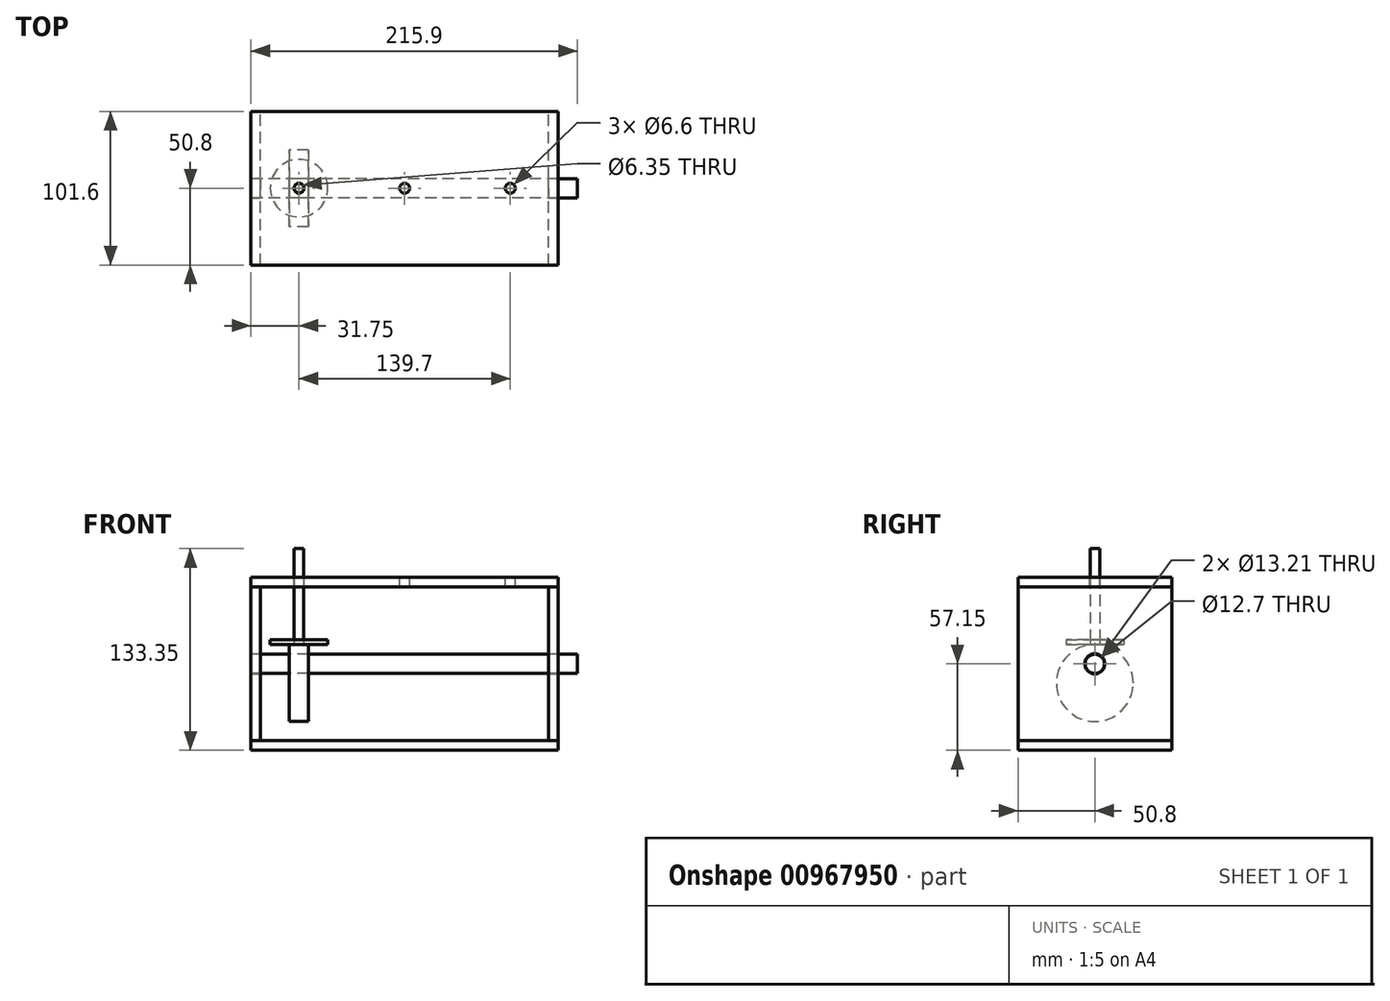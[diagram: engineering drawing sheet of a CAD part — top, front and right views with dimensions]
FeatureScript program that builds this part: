
annotation { "Feature Type Name" : "Feature", "Feature Type Description" : "" }
export const myFeature = defineFeature(function(context is Context, id is Id, definition is map)
    precondition{}
    {
        {
            assignVariable(context, id + "F0", {"name" : "thickness", "anyValue" : 101.6 * mm});
        }
        {
            var Q0;
            Q0=qCreatedBy(makeId("Front.planeOp"),FACE);
            var sketch = newSketch(context, id + "F1", { "sketchPlane" : qUnion([Q0])});
            skLineSegment(sketch, "E0.bottom", {"start": v(-101.6, 6.35) * mm, "end": v(101.6, 6.35) * mm});
            skLineSegment(sketch, "E0.top", {"start": v(-101.6, 0) * mm, "end": v(101.6, 0) * mm});
            skLineSegment(sketch, "E0.left", {"start": v(-101.6, 6.35) * mm, "end": v(-101.6, 0) * mm});
            skLineSegment(sketch, "E0.right", {"start": v(101.6, 6.35) * mm, "end": v(101.6, 0) * mm});
            skLineSegment(sketch, "E1", {"start": v(-101.6, 6.35) * mm, "end": v(-101.6, 107.95) * mm});
            skLineSegment(sketch, "E2", {"start": v(-101.6, 107.95) * mm, "end": v(101.6, 107.95) * mm});
            skLineSegment(sketch, "E3", {"start": v(101.6, 107.95) * mm, "end": v(101.6, 6.35) * mm});
            skLineSegment(sketch, "E4", {"start": v(-95.25, 6.35) * mm, "end": v(-95.25, 107.95) * mm});
            skLineSegment(sketch, "E5", {"start": v(95.25, 6.35) * mm, "end": v(95.25, 107.95) * mm});
            skLineSegment(sketch, "E6", {"start": v(-95.25, 57.15) * mm, "end": v(-101.6, 57.15) * mm, "construction": true});
            skLineSegment(sketch, "E7", {"start": v(95.25, 57.15) * mm, "end": v(101.6, 57.15) * mm, "construction": true});
            skLineSegment(sketch, "E8", {"start": v(-101.6, 107.95) * mm, "end": v(-101.6, 114.3) * mm});
            skLineSegment(sketch, "E9", {"start": v(-101.6, 114.3) * mm, "end": v(101.6, 114.3) * mm});
            skLineSegment(sketch, "E10", {"start": v(101.6, 114.3) * mm, "end": v(101.6, 107.95) * mm});
            skLineSegment(sketch, "E11", {"start": v(-95.25, 57.15) * mm, "end": v(-69.85, 57.15) * mm});
            skLineSegment(sketch, "E12", {"start": v(-69.85, 57.15) * mm, "end": v(0, 57.15) * mm});
            skLineSegment(sketch, "E13", {"start": v(0, 57.15) * mm, "end": v(69.85, 57.15) * mm});
            skLineSegment(sketch, "E14", {"start": v(69.85, 57.15) * mm, "end": v(95.25, 57.15) * mm});
            skLineSegment(sketch, "E15", {"start": v(-69.85, 57.15) * mm, "end": v(-69.85, 44.45) * mm, "construction": true});
            skLineSegment(sketch, "E16", {"start": v(0, 63.5) * mm, "end": v(0, 57.15) * mm, "construction": true});
            skLineSegment(sketch, "E17", {"start": v(69.85, 57.15) * mm, "end": v(69.85, 63.5) * mm, "construction": true});
            skLineSegment(sketch, "E18.bottom", {"start": v(-63.5, 69.85) * mm, "end": v(-76.2, 69.85) * mm});
            skLineSegment(sketch, "E18.top", {"start": v(-63.5, 19.05) * mm, "end": v(-76.2, 19.05) * mm});
            skLineSegment(sketch, "E18.left", {"start": v(-63.5, 69.85) * mm, "end": v(-63.5, 19.05) * mm});
            skLineSegment(sketch, "E18.right", {"start": v(-76.2, 69.85) * mm, "end": v(-76.2, 19.05) * mm});
            skPoint(sketch, "E18.middle", {"position": v(-69.85, 44.45) * mm});
            skLineSegment(sketch, "E19.bottom", {"start": v(6.35, 38.1) * mm, "end": v(-6.35, 38.1) * mm});
            skLineSegment(sketch, "E19.top", {"start": v(6.35, 88.9) * mm, "end": v(-6.35, 88.9) * mm});
            skLineSegment(sketch, "E19.left", {"start": v(6.35, 38.1) * mm, "end": v(6.35, 88.9) * mm});
            skLineSegment(sketch, "E19.right", {"start": v(-6.35, 38.1) * mm, "end": v(-6.35, 88.9) * mm});
            skPoint(sketch, "E19.middle", {"position": v(0, 63.5) * mm});
            skLineSegment(sketch, "E20.bottom", {"start": v(63.5, 38.1) * mm, "end": v(76.2, 38.1) * mm});
            skLineSegment(sketch, "E20.top", {"start": v(63.5, 88.9) * mm, "end": v(76.2, 88.9) * mm});
            skLineSegment(sketch, "E20.left", {"start": v(63.5, 38.1) * mm, "end": v(63.5, 88.9) * mm});
            skLineSegment(sketch, "E20.right", {"start": v(76.2, 38.1) * mm, "end": v(76.2, 88.9) * mm});
            skPoint(sketch, "E20.middle", {"position": v(69.85, 63.5) * mm});
            skLineSegment(sketch, "E21", {"start": v(-76.2, 44.45) * mm, "end": v(-63.5, 44.45) * mm});
            skLineSegment(sketch, "E22", {"start": v(-6.35, 63.5) * mm, "end": v(6.35, 63.5) * mm});
            skLineSegment(sketch, "E23", {"start": v(63.5, 63.5) * mm, "end": v(76.2, 63.5) * mm});
            skLineSegment(sketch, "E24", {"start": v(-69.85, 69.85) * mm, "end": v(-69.85, 133.35) * mm, "construction": true});
            skLineSegment(sketch, "E25", {"start": v(0, 88.9) * mm, "end": v(0, 152.4) * mm, "construction": true});
            skLineSegment(sketch, "E26", {"start": v(69.85, 88.9) * mm, "end": v(69.85, 152.4) * mm, "construction": true});
            skSolve(sketch);
        }
        {
            var Q0;
            Q0=makeQuery(id+"F1.imprint","IMPRINT",FACE,{"disambiguationData":[TD([[makeQuery(id+"F1.imprint","IMPRINT",EDGE,{"derivedFrom":sQuery(id+"F1.wireOp",EDGE,"E0.top")}),1.0]])]});
            var Q1;
            {var subQ0=sQuery(id+"F1.wireOp",EDGE,"E8");Q1=makeQuery(id+"F1.imprint","IMPRINT",FACE,{"disambiguationData":[TD([[makeQuery(id+"F1.imprint","IMPRINT",EDGE,{"derivedFrom":subQ0}),-1.0]])]});}
            extrude(context, id + "F2", {"entities" : qUnion([Q0, Q1]), "endBound" : BoundingType.SYMMETRIC, "depth" : getVariable(context, 'thickness'), "offsetDistance" : 25.4 * mm});
        }
        {
            var Q0;
            {var subQ1=sQuery(id+"F1.wireOp",EDGE,"E1");Q0=makeQuery(id+"F1.imprint","IMPRINT",FACE,{"disambiguationData":[TD([[makeQuery(id+"F1.imprint","IMPRINT",EDGE,{"derivedFrom":subQ1}),-1.0]])]});}
            var Q1;
            {var subQ4=sQuery(id+"F1.wireOp",EDGE,"E3");Q1=makeQuery(id+"F1.imprint","IMPRINT",FACE,{"disambiguationData":[TD([[makeQuery(id+"F1.imprint","IMPRINT",EDGE,{"derivedFrom":subQ4}),-1.0]])]});}
            var Q2;
            Q2=makeQuery(id+"F2.opExtrude","CAP_FACE",FACE,{"disambiguationData":[OSD([sQuery(id+"F1.wireOp",EDGE,"E2"),sQuery(id+"F1.wireOp",EDGE,"E8"),sQuery(id+"F1.wireOp",EDGE,"E9"),sQuery(id+"F1.wireOp",EDGE,"E10")])],"isStart":false});
            var Q3;
            Q3=makeQuery(id+"F2.opExtrude","CAP_FACE",FACE,{"disambiguationData":[OSD([sQuery(id+"F1.wireOp",EDGE,"E2"),sQuery(id+"F1.wireOp",EDGE,"E8"),sQuery(id+"F1.wireOp",EDGE,"E9"),sQuery(id+"F1.wireOp",EDGE,"E10")])],"isStart":true});
            extrude(context, id + "F3", {"entities" : qUnion([Q0, Q1]), "endBound" : BoundingType.UP_TO_SURFACE, "depth" : 25.4 * mm, "endBoundEntityFace" : qUnion([Q2]), "offsetDistance" : 25.4 * mm, "hasSecondDirection" : true, "secondDirectionBound" : SecondDirectionBoundingType.UP_TO_SURFACE, "secondDirectionOppositeDirection" : true, "secondDirectionDepth" : 25.4 * mm, "secondDirectionBoundEntityFace" : qUnion([Q3])});
        }
        {
            var Q0;
            Q0=makeQuery(id+"F3.opExtrude","SWEPT_FACE",FACE,{"disambiguationData":[OSD([sQuery(id+"F1.wireOp",EDGE,"E3")])]});
            var sketch = newSketch(context, id + "F4", { "sketchPlane" : qUnion([Q0])});
            skCircle(sketch, "E27", {"center": v(0, 57.15) * mm, "radius": 6.6 * mm});
            skCircle(sketch, "E28", {"center": v(0, 57.15) * mm, "radius": 6.35 * mm});
            skSolve(sketch);
        }
        {
            var Q0;
            Q0=makeQuery(id+"F4.imprint","IMPRINT",FACE,{"disambiguationData":[TD([[makeQuery(id+"F4.imprint","IMPRINT",EDGE,{"derivedFrom":sQuery(id+"F4.wireOp",EDGE,"E28")}),1.0]])]});
            var Q1;
            Q1=makeQuery(id+"F4.imprint","IMPRINT",FACE,{"disambiguationData":[TD([[makeQuery(id+"F4.imprint","IMPRINT",EDGE,{"derivedFrom":sQuery(id+"F4.wireOp",EDGE,"E27")}),1.0]])]});
            extrude(context, id + "F5", {"entities" : qUnion([Q0, Q1]), "operationType" : NewBodyOperationType.REMOVE, "endBound" : BoundingType.THROUGH_ALL, "oppositeDirection" : true, "depth" : 25.4 * mm, "offsetDistance" : 25.4 * mm});
        }
        {
            var Q0;
            Q0=makeQuery(id+"F4.imprint","IMPRINT",FACE,{"disambiguationData":[TD([[makeQuery(id+"F4.imprint","IMPRINT",EDGE,{"derivedFrom":sQuery(id+"F4.wireOp",EDGE,"E28")}),1.0]])]});
            var Q1;
            Q1=makeQuery(id+"F3.opExtrude","SWEPT_FACE",FACE,{"disambiguationData":[OSD([sQuery(id+"F1.wireOp",EDGE,"E1")])]});
            extrude(context, id + "F6", {"entities" : qUnion([Q0]), "depth" : 12.7 * mm, "offsetDistance" : 25.4 * mm, "hasSecondDirection" : true, "secondDirectionBound" : SecondDirectionBoundingType.UP_TO_SURFACE, "secondDirectionOppositeDirection" : true, "secondDirectionDepth" : 25.4 * mm, "secondDirectionBoundEntityFace" : qUnion([Q1])});
        }
        {
            var Q0;
            {var subQ0=sQuery(id+"F1.wireOp",EDGE,"E18.top");Q0=makeQuery(id+"F1.imprint","IMPRINT",FACE,{"disambiguationData":[TD([[makeQuery(id+"F1.imprint","IMPRINT",EDGE,{"derivedFrom":subQ0}),-1.0]])]});}
            var Q1;
            Q1=sQuery(id+"F1.wireOp",EDGE,"E21");
            revolve(context, id + "F7", {"surfaceOperationType" : NewSurfaceOperationType.NEW, "entities" : qUnion([Q0]), "axis" : qUnion([Q1]), "revolveType" : RevolveType.FULL});
        }
        {
            var Q0;
            Q0=makeQuery(id+"F6.opExtrude","SWEPT_BODY",BODY,{"disambiguationData":[OSD([sQuery(id+"F4.wireOp",EDGE,"E28")])]});
            var Q1;
            Q1=makeQuery(id+"F7.opRevolve","SWEPT_BODY",BODY,{"disambiguationData":[OSD([sQuery(id+"F1.wireOp",EDGE,"E18.top"),sQuery(id+"F1.wireOp",EDGE,"E18.left"),sQuery(id+"F1.wireOp",EDGE,"E18.right"),sQuery(id+"F1.wireOp",EDGE,"E21")])]});
            booleanBodies(context, id + "F8", {"operationType" : BooleanOperationType.SUBTRACTION, "tools" : qUnion([Q0]), "targets" : qUnion([Q1]), "keepTools" : true});
        }
        {
            var Q0;
            Q0=makeQuery(id+"F2.opExtrude","SWEPT_FACE",FACE,{"disambiguationData":[OSD([sQuery(id+"F1.wireOp",EDGE,"E9")])]});
            var sketch = newSketch(context, id + "F9", { "sketchPlane" : qUnion([Q0])});
            skPoint(sketch, "E29", {"position": v(0, 0) * mm});
            skPoint(sketch, "E30", {"position": v(-69.85, 0) * mm});
            skPoint(sketch, "E31", {"position": v(69.85, 0) * mm});
            skSolve(sketch);
        }
        {
            var Q0;
            Q0=sQuery(id+"F9.wireOp",VERTEX,"E30");
            var Q1;
            Q1=sQuery(id+"F9.wireOp",VERTEX,"E29");
            var Q2;
            Q2=sQuery(id+"F9.wireOp",VERTEX,"E31");
            var Q3;
            Q3=makeQuery(id+"F2.opExtrude","SWEPT_BODY",BODY,{"disambiguationData":[OSD([sQuery(id+"F1.wireOp",EDGE,"E2"),sQuery(id+"F1.wireOp",EDGE,"E8"),sQuery(id+"F1.wireOp",EDGE,"E9"),sQuery(id+"F1.wireOp",EDGE,"E10")])]});
            hole(context, id + "F10", {"style" : HoleStyle.SIMPLE, "endStyle" : HoleEndStyle.THROUGH, "holeDiameter" : 6.6 * mm, "majorDiameter" : 3.5 * mm, "isTappedThrough" : true, "tappedDepth" : 12.7 * mm, "tapClearance" : 3, "startFromSketch" : true, "locations" : qUnion([Q0, Q1, Q2]), "scope" : qUnion([Q3])});
        }
        {
            var Q0;
            Q0=sQuery(id+"F1.wireOp",VERTEX,"E24.start");
            var Q1;
            Q1=qCreatedBy(makeId("Top.planeOp"),FACE);
            cPlane(context, id + "F11", {"entities" : qUnion([Q0, Q1]), "cplaneType" : CPlaneType.PLANE_POINT, "offset" : 25.4 * mm, "width" : 152.4 * mm, "height" : 152.4 * mm});
        }
        {
            var Q0;
            Q0=qCreatedBy(id+"F11.planeOp",FACE);
            var sketch = newSketch(context, id + "F12", { "sketchPlane" : qUnion([Q0])});
            skCircle(sketch, "E32", {"center": v(-69.85, 0) * mm, "radius": 3.18 * mm});
            skCircle(sketch, "E33", {"center": v(-69.85, 0) * mm, "radius": 19.05 * mm});
            skSolve(sketch);
        }
        {
            var Q0;
            Q0=makeQuery(id+"F12.imprint","IMPRINT",FACE,{"disambiguationData":[TD([[makeQuery(id+"F12.imprint","IMPRINT",EDGE,{"derivedFrom":sQuery(id+"F12.wireOp",EDGE,"E32")}),1.0]])]});
            var Q1;
            Q1=sQuery(id+"F1.wireOp",VERTEX,"E24.end");
            extrude(context, id + "F13", {"entities" : qUnion([Q0]), "endBound" : BoundingType.UP_TO_VERTEX, "depth" : 25.4 * mm, "endBoundEntityVertex" : qUnion([Q1]), "offsetDistance" : 25.4 * mm});
        }
        {
            var Q0;
            Q0=makeQuery(id+"F12.imprint","IMPRINT",FACE,{"disambiguationData":[TD([[makeQuery(id+"F12.imprint","IMPRINT",EDGE,{"derivedFrom":sQuery(id+"F12.wireOp",EDGE,"E32")}),-1.0]])]});
            extrude(context, id + "F14", {"entities" : qUnion([Q0]), "depth" : 3.17 * mm, "offsetDistance" : 25.4 * mm});
        }
    });
